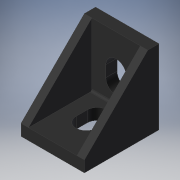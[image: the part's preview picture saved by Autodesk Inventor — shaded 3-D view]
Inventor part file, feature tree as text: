
AUTODESK INVENTOR PART (.ipt)
format: ipt  version: 2019 (Build 230136000, 136)  size: 150,528 bytes
history: native  units: mm
features: extrude x7, sketch x7
ambient origin geometry x8: Origin, YZ Plane, XZ Plane, XY Plane, X Axis, Y Axis, Z Axis, Center Point
bodies: Solid1 (feature_tree)
feature tree (14):
  extrude  "Extrusion1"  Depth=13.0mm TaperAngle=0.0deg
  extrude  "Extrusion2"  Depth=12.0mm TaperAngle=0.0deg
  extrude  "Extrusion3"  Depth=12.0mm TaperAngle=0.0deg
  extrude  "Extrusion4"  [1 undecoded]
  extrude  "Extrusion5"  [1 undecoded]
  extrude  "Extrusion6"  [1 undecoded]
  extrude  "Extrusion7"  [1 undecoded]
  sketch  "Sketch_1"  dims[d0=17.0mm d1=0.0mm d2=13.0mm d3=0.0mm]
  sketch  "Sketch_2"  dims[d4=12.0mm d5=0.0mm d6=12.0mm d7=0.0mm]
  sketch  "Sketch_3"  dims[d8=12.0mm d9=0.0mm d10=5.0mm d11=0.0mm]
  sketch  "Sketch_4"  dims[d12=5.0mm d13=0.0mm]
  sketch  "Sketch_5"
  sketch  "Sketch_10"
  sketch  "Sketch_11"
note: 4 required parameter values undecoded (feature->parameter linkage not recoverable at this tier; creation-order binding heuristic only, values carry confidence <= 0.55)
